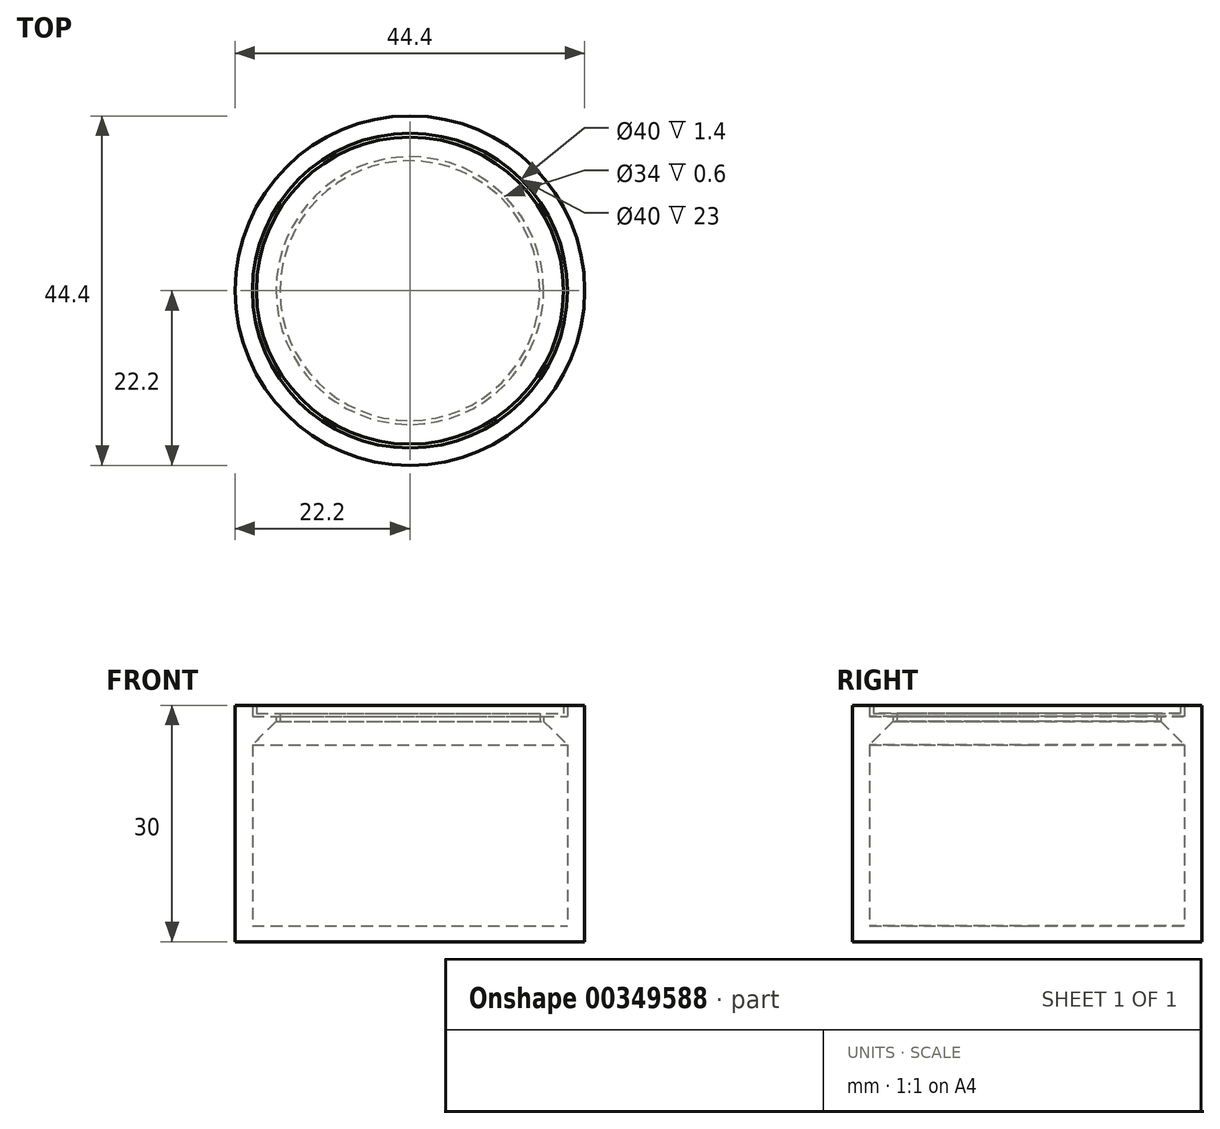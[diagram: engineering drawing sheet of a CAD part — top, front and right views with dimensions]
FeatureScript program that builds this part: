
annotation { "Feature Type Name" : "Feature", "Feature Type Description" : "" }
export const myFeature = defineFeature(function(context is Context, id is Id, definition is map)
    precondition{}
    {
        {
            var Q0;
            Q0=qCreatedBy(makeId("Right.planeOp"),FACE);
            var sketch = newSketch(context, id + "F0", { "sketchPlane" : qUnion([Q0])});
            skLineSegment(sketch, "E0", {"start": v(22.2, 0) * mm, "end": v(22.2, -30) * mm});
            skLineSegment(sketch, "E1", {"start": v(22.2, -30) * mm, "end": v(0, -30) * mm});
            skLineSegment(sketch, "E2", {"start": v(0, -30) * mm, "end": v(0, -28) * mm});
            skLineSegment(sketch, "E3", {"start": v(0, -28) * mm, "end": v(20, -28) * mm});
            skLineSegment(sketch, "E4", {"start": v(20, -28) * mm, "end": v(20, -5) * mm});
            skLineSegment(sketch, "E5", {"start": v(17, -1.4) * mm, "end": v(20, -1.4) * mm});
            skLineSegment(sketch, "E6", {"start": v(20, -1.4) * mm, "end": v(20, 0) * mm});
            skLineSegment(sketch, "E7", {"start": v(20, 0) * mm, "end": v(22.2, 0) * mm});
            skLineSegment(sketch, "E8", {"start": v(19.5, 0) * mm, "end": v(0, 0) * mm});
            skLineSegment(sketch, "E9", {"start": v(0, 0) * mm, "end": v(0, -2) * mm});
            skLineSegment(sketch, "E10", {"start": v(0, -2) * mm, "end": v(16.5, -2) * mm});
            skLineSegment(sketch, "E11", {"start": v(16.5, -2) * mm, "end": v(16.5, -1) * mm});
            skLineSegment(sketch, "E12", {"start": v(16.5, -1) * mm, "end": v(19.5, -1) * mm});
            skLineSegment(sketch, "E13", {"start": v(19.5, -1) * mm, "end": v(19.5, 0) * mm});
            skLineSegment(sketch, "E14", {"start": v(17, -1.4) * mm, "end": v(17, -2) * mm});
            skLineSegment(sketch, "E15", {"start": v(17, -2) * mm, "end": v(20, -5) * mm});
            skSolve(sketch);
        }
        {
            var Q0;
            Q0=makeQuery(id+"F0.imprint","IMPRINT",FACE,{"disambiguationData":[TD([[makeQuery(id+"F0.imprint","IMPRINT",EDGE,{"derivedFrom":sQuery(id+"F0.wireOp",EDGE,"E0")}),-1.0]])]});
            var Q1;
            Q1=makeQuery(id+"F0.imprint","IMPRINT",FACE,{"disambiguationData":[TD([[makeQuery(id+"F0.imprint","IMPRINT",EDGE,{"derivedFrom":sQuery(id+"F0.wireOp",EDGE,"E8")}),1.0]])]});
            var Q2;
            Q2=sQuery(id+"F0.wireOp",EDGE,"E2");
            revolve(context, id + "F1", {"entities" : qUnion([Q0, Q1]), "axis" : qUnion([Q2]), "revolveType" : RevolveType.FULL});
        }
    });
